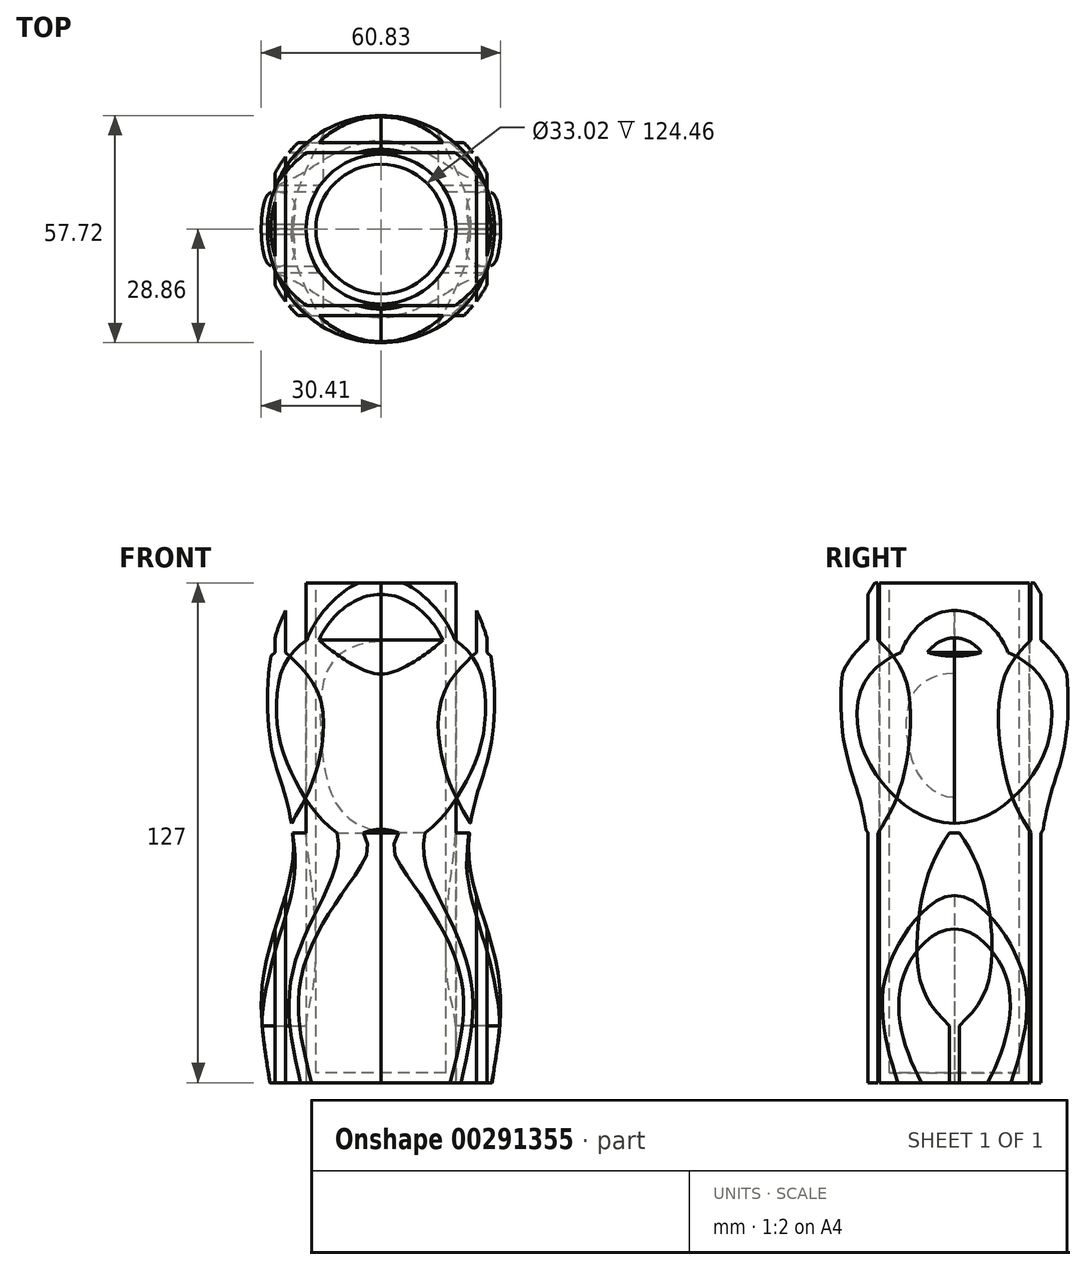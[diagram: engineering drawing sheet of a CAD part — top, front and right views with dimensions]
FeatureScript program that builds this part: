
annotation { "Feature Type Name" : "Feature", "Feature Type Description" : "" }
export const myFeature = defineFeature(function(context is Context, id is Id, definition is map)
    precondition{}
    {
        {
            var Q0;
            Q0=qCreatedBy(makeId("Right.planeOp"),FACE);
            var sketch = newSketch(context, id + "F0", { "sketchPlane" : qUnion([Q0])});
            skLineSegment(sketch, "E0.bottom", {"start": v(44.45, 63.5) * mm, "end": v(-44.45, 63.5) * mm});
            skLineSegment(sketch, "E0.top", {"start": v(44.45, -63.5) * mm, "end": v(-44.45, -63.5) * mm});
            skLineSegment(sketch, "E0.left", {"start": v(44.45, 63.5) * mm, "end": v(44.45, -63.5) * mm});
            skLineSegment(sketch, "E0.right", {"start": v(-44.45, 63.5) * mm, "end": v(-44.45, -63.5) * mm});
            skPoint(sketch, "E0.middle", {"position": v(0, 0) * mm});
            skLineSegment(sketch, "E1", {"start": v(0, 63.5) * mm, "end": v(-1.27, 63.5) * mm});
            skLineSegment(sketch, "E2", {"start": v(-1.27, 63.5) * mm, "end": v(-1.27, 0) * mm});
            skFitSpline(sketch, "E3", {"points": [v(-1.27, 0) * mm, v(-7.1, -11.9) * mm, v(-8.58, -38.04) * mm, v(-1.27, -49.01) * mm], "startDerivative": vector(-21.64, -33.6) * mm, "endDerivative": vector(30.34, -30.06) * mm});
            skLineSegment(sketch, "E4", {"start": v(-1.27, -49.01) * mm, "end": v(-1.27, -63.5) * mm});
            skLineSegment(sketch, "E5.MirrorCS", {"start": v(1.27, 63.5) * mm, "end": v(1.27, 0) * mm});
            skFitSpline(sketch, "E6.MirrorCS", {"points": [v(1.27, 0) * mm, v(7.1, -11.9) * mm, v(8.58, -38.04) * mm, v(1.27, -49.01) * mm], "startDerivative": vector(21.64, -33.6) * mm, "endDerivative": vector(-30.34, -30.06) * mm});
            skLineSegment(sketch, "E7.MirrorCS", {"start": v(1.27, -49.01) * mm, "end": v(1.27, -63.5) * mm});
            skPoint(sketch, "E8.end.orphan", {"position": v(0, -63.5) * mm});
            skLineSegment(sketch, "E9", {"start": v(-1.27, 0) * mm, "end": v(1.27, 0) * mm});
            skFitSpline(sketch, "E10.MirrorCS", {"points": [v(19.47, 0) * mm, v(13.64, 11.9) * mm, v(12.16, 38.04) * mm, v(19.47, 49.01) * mm], "startDerivative": vector(-21.64, 33.6) * mm, "endDerivative": vector(30.34, 30.06) * mm});
            skPoint(sketch, "E11.end.orphan", {"position": v(10.37, 0) * mm});
            skPoint(sketch, "E12.MirrorCS.end.orphan", {"position": v(1.27, 49.01) * mm});
            skPoint(sketch, "E13.trimOffspring.end.orphan", {"position": v(44.45, 0) * mm});
            skPoint(sketch, "E14.orphan", {"position": v(-44.45, 0) * mm});
            skLineSegment(sketch, "E15", {"start": v(19.47, 49.01) * mm, "end": v(19.47, 63.5) * mm});
            skLineSegment(sketch, "E16", {"start": v(19.47, 0) * mm, "end": v(19.47, -63.5) * mm});
            skLineSegment(sketch, "E17", {"start": v(19.47, -63.5) * mm, "end": v(20.74, -63.5) * mm});
            skLineSegment(sketch, "E18.MirrorCS", {"start": v(22.01, 49.01) * mm, "end": v(22.01, 63.5) * mm});
            skFitSpline(sketch, "E19.MirrorCS", {"points": [v(22.01, 0) * mm, v(27.84, 11.9) * mm, v(29.32, 38.04) * mm, v(22.01, 49.01) * mm], "startDerivative": vector(21.64, 33.6) * mm, "endDerivative": vector(-30.34, 30.06) * mm});
            skLineSegment(sketch, "E20.MirrorCS", {"start": v(22.01, 0) * mm, "end": v(22.01, -63.5) * mm});
            skPoint(sketch, "E21.end.orphan", {"position": v(20.74, 63.5) * mm});
            skFitSpline(sketch, "E22.MirrorCS", {"points": [v(-19.47, 0) * mm, v(-13.64, 11.9) * mm, v(-12.16, 38.04) * mm, v(-19.47, 49.01) * mm], "startDerivative": vector(21.64, 33.6) * mm, "endDerivative": vector(-30.34, 30.06) * mm});
            skFitSpline(sketch, "E23.MirrorCS", {"points": [v(-22.01, 0) * mm, v(-27.84, 11.9) * mm, v(-29.32, 38.04) * mm, v(-22.01, 49.01) * mm], "startDerivative": vector(-21.64, 33.6) * mm, "endDerivative": vector(30.34, 30.06) * mm});
            skLineSegment(sketch, "E24.MirrorCS", {"start": v(-22.01, 49.01) * mm, "end": v(-22.01, 63.5) * mm});
            skLineSegment(sketch, "E25.MirrorCS", {"start": v(-19.47, 49.01) * mm, "end": v(-19.47, 63.5) * mm});
            skLineSegment(sketch, "E26.MirrorCS", {"start": v(-19.47, 0) * mm, "end": v(-19.47, -63.5) * mm});
            skLineSegment(sketch, "E27.MirrorCS", {"start": v(-22.01, 0) * mm, "end": v(-22.01, -63.5) * mm});
            skSolve(sketch);
        }
        {
            var Q0;
            Q0=makeQuery(id+"F0.imprint","IMPRINT",FACE,{"disambiguationData":[TD([[makeQuery(id+"F0.imprint","IMPRINT",EDGE,{"derivedFrom":sQuery(id+"F0.wireOp",EDGE,"E22.MirrorCS")}),1.0]])]});
            var Q1;
            {var subQ1=sQuery(id+"F0.wireOp",EDGE,"E1");Q1=makeQuery(id+"F0.imprint","IMPRINT",FACE,{"disambiguationData":[TD([[makeQuery(id+"F0.imprint","IMPRINT",EDGE,{"derivedFrom":subQ1}),1.0]])]});}
            var Q2;
            Q2=makeQuery(id+"F0.imprint","IMPRINT",FACE,{"disambiguationData":[TD([[makeQuery(id+"F0.imprint","IMPRINT",EDGE,{"derivedFrom":sQuery(id+"F0.wireOp",EDGE,"E3")}),1.0]])]});
            var Q3;
            Q3=makeQuery(id+"F0.imprint","IMPRINT",FACE,{"disambiguationData":[TD([[makeQuery(id+"F0.imprint","IMPRINT",EDGE,{"derivedFrom":sQuery(id+"F0.wireOp",EDGE,"E10.MirrorCS")}),-1.0]])]});
            extrude(context, id + "F1", {"entities" : qUnion([Q0, Q1, Q2, Q3]), "depth" : 31.75 * mm});
        }
        {
            var Q0;
            Q0=makeQuery(id+"F1.opExtrude","CAP_FACE",FACE,{"disambiguationData":[OSD([sQuery(id+"F0.wireOp",EDGE,"E0.bottom"),sQuery(id+"F0.wireOp",EDGE,"E0.top"),sQuery(id+"F0.wireOp",EDGE,"E22.MirrorCS"),sQuery(id+"F0.wireOp",EDGE,"E23.MirrorCS"),sQuery(id+"F0.wireOp",EDGE,"E24.MirrorCS"),sQuery(id+"F0.wireOp",EDGE,"E25.MirrorCS"),sQuery(id+"F0.wireOp",EDGE,"E26.MirrorCS"),sQuery(id+"F0.wireOp",EDGE,"E27.MirrorCS")])],"isStart":true});
            var Q1;
            Q1=makeQuery(id+"F1.opExtrude","CAP_FACE",FACE,{"disambiguationData":[OSD([sQuery(id+"F0.wireOp",EDGE,"E0.bottom"),sQuery(id+"F0.wireOp",EDGE,"E0.top"),sQuery(id+"F0.wireOp",EDGE,"E1"),sQuery(id+"F0.wireOp",EDGE,"E2"),sQuery(id+"F0.wireOp",EDGE,"E3"),sQuery(id+"F0.wireOp",EDGE,"E4"),sQuery(id+"F0.wireOp",EDGE,"E5.MirrorCS"),sQuery(id+"F0.wireOp",EDGE,"E6.MirrorCS"),sQuery(id+"F0.wireOp",EDGE,"E7.MirrorCS")])],"isStart":true});
            var Q2;
            Q2=makeQuery(id+"F1.opExtrude","CAP_FACE",FACE,{"disambiguationData":[OSD([sQuery(id+"F0.wireOp",EDGE,"E0.bottom"),sQuery(id+"F0.wireOp",EDGE,"E0.top"),sQuery(id+"F0.wireOp",EDGE,"E10.MirrorCS"),sQuery(id+"F0.wireOp",EDGE,"E15"),sQuery(id+"F0.wireOp",EDGE,"E16"),sQuery(id+"F0.wireOp",EDGE,"E17"),sQuery(id+"F0.wireOp",EDGE,"E18.MirrorCS"),sQuery(id+"F0.wireOp",EDGE,"E19.MirrorCS"),sQuery(id+"F0.wireOp",EDGE,"E20.MirrorCS")])],"isStart":true});
            extrude(context, id + "F2", {"entities" : qUnion([Q0, Q1, Q2]), "depth" : 31.75 * mm});
        }
        {
            var Q0;
            Q0=qCreatedBy(makeId("Front.planeOp"),FACE);
            var sketch = newSketch(context, id + "F3", { "sketchPlane" : qUnion([Q0])});
            skLineSegment(sketch, "E28.bottom", {"start": v(63.5, 63.5) * mm, "end": v(-63.5, 63.5) * mm});
            skLineSegment(sketch, "E28.top", {"start": v(63.5, -63.5) * mm, "end": v(-63.5, -63.5) * mm});
            skLineSegment(sketch, "E28.left", {"start": v(63.5, 63.5) * mm, "end": v(63.5, -63.5) * mm});
            skLineSegment(sketch, "E28.right", {"start": v(-63.5, 63.5) * mm, "end": v(-63.5, -63.5) * mm});
            skPoint(sketch, "E28.middle", {"position": v(0, 0) * mm});
            skLineSegment(sketch, "E29", {"start": v(0, 63.5) * mm, "end": v(1.27, 63.5) * mm});
            skLineSegment(sketch, "E30", {"start": v(1.27, 63.5) * mm, "end": v(1.27, 0) * mm});
            skLineSegment(sketch, "E31", {"start": v(0, 0) * mm, "end": v(1.27, 0) * mm});
            skFitSpline(sketch, "E32", {"points": [v(1.27, 0) * mm, v(8.62, -14.28) * mm, v(10.1, -34) * mm, v(1.27, -45.84) * mm], "startDerivative": vector(25.04, -39.95) * mm, "endDerivative": vector(-35.1, -33.02) * mm});
            skLineSegment(sketch, "E33.trimOffspring", {"start": v(1.27, -45.84) * mm, "end": v(1.27, -63.5) * mm});
            skLineSegment(sketch, "E34.MirrorCS", {"start": v(-1.27, 63.5) * mm, "end": v(-1.27, 0) * mm});
            skFitSpline(sketch, "E35.MirrorCS", {"points": [v(-1.27, 0) * mm, v(-8.62, -14.28) * mm, v(-10.1, -34) * mm, v(-1.27, -45.84) * mm], "startDerivative": vector(-25.04, -39.95) * mm, "endDerivative": vector(35.1, -33.02) * mm});
            skLineSegment(sketch, "E36.MirrorCS", {"start": v(-1.27, -45.84) * mm, "end": v(-1.27, -63.5) * mm});
            skPoint(sketch, "E37.end.orphan", {"position": v(0, -63.5) * mm});
            skFitSpline(sketch, "E38.MirrorCS", {"points": [v(24.24, 0) * mm, v(16.9, 14.28) * mm, v(15.41, 34) * mm, v(24.24, 45.84) * mm], "startDerivative": vector(-25.04, 39.95) * mm, "endDerivative": vector(35.1, 33.02) * mm});
            skPoint(sketch, "E39.trimOffspring.end.orphan", {"position": v(63.5, 0) * mm});
            skPoint(sketch, "E40.orphan", {"position": v(-63.5, 0) * mm});
            skLineSegment(sketch, "E41", {"start": v(24.24, 45.84) * mm, "end": v(24.24, 63.5) * mm});
            skLineSegment(sketch, "E42", {"start": v(24.24, 63.5) * mm, "end": v(25.5, 63.5) * mm});
            skLineSegment(sketch, "E43", {"start": v(24.24, 0) * mm, "end": v(24.24, -63.5) * mm});
            skFitSpline(sketch, "E44.MirrorCS", {"points": [v(26.91, 0) * mm, v(34.26, 14.28) * mm, v(35.74, 34) * mm, v(26.91, 45.84) * mm], "startDerivative": vector(25.04, 39.95) * mm, "endDerivative": vector(-35.1, 33.02) * mm});
            skLineSegment(sketch, "E45.MirrorCS", {"start": v(26.91, 45.84) * mm, "end": v(26.91, 63.5) * mm});
            skLineSegment(sketch, "E46.MirrorCS", {"start": v(26.91, 0) * mm, "end": v(26.91, -63.5) * mm});
            skPoint(sketch, "E47.MirrorCS.end.orphan", {"position": v(1.27, 45.84) * mm});
            skLineSegment(sketch, "E48.MirrorCS", {"start": v(-24.24, 45.84) * mm, "end": v(-24.24, 63.5) * mm});
            skFitSpline(sketch, "E49.MirrorCS", {"points": [v(-24.24, 0) * mm, v(-16.9, 14.28) * mm, v(-15.41, 34) * mm, v(-24.24, 45.84) * mm], "startDerivative": vector(25.04, 39.95) * mm, "endDerivative": vector(-35.1, 33.02) * mm});
            skFitSpline(sketch, "E50.MirrorCS", {"points": [v(-26.91, 0) * mm, v(-34.26, 14.28) * mm, v(-35.74, 34) * mm, v(-26.91, 45.84) * mm], "startDerivative": vector(-25.04, 39.95) * mm, "endDerivative": vector(35.1, 33.02) * mm});
            skLineSegment(sketch, "E51.MirrorCS", {"start": v(-26.91, 0) * mm, "end": v(-26.91, -63.5) * mm});
            skLineSegment(sketch, "E52.MirrorCS", {"start": v(-24.24, 0) * mm, "end": v(-24.24, -63.5) * mm});
            skLineSegment(sketch, "E53", {"start": v(-26.91, 45.84) * mm, "end": v(-26.91, 63.5) * mm});
            skSolve(sketch);
        }
        {
            var Q0;
            Q0=makeQuery(id+"F3.imprint","IMPRINT",FACE,{"disambiguationData":[TD([[makeQuery(id+"F3.imprint","IMPRINT",EDGE,{"derivedFrom":sQuery(id+"F3.wireOp",EDGE,"E38.MirrorCS")}),-1.0]])]});
            var Q1;
            {var subQ0=sQuery(id+"F3.wireOp",EDGE,"E29");Q1=makeQuery(id+"F3.imprint","IMPRINT",FACE,{"disambiguationData":[TD([[makeQuery(id+"F3.imprint","IMPRINT",EDGE,{"derivedFrom":subQ0}),-1.0]])]});}
            var Q2;
            {var subQ3=sQuery(id+"F3.wireOp",EDGE,"E48.MirrorCS");Q2=makeQuery(id+"F3.imprint","IMPRINT",FACE,{"disambiguationData":[TD([[makeQuery(id+"F3.imprint","IMPRINT",EDGE,{"derivedFrom":subQ3}),1.0]])]});}
            extrude(context, id + "F4", {"entities" : qUnion([Q0, Q1, Q2]), "depth" : 31.75 * mm});
        }
        {
            var Q0;
            Q0=makeQuery(id+"F4.opExtrude","CAP_FACE",FACE,{"disambiguationData":[OSD([sQuery(id+"F3.wireOp",EDGE,"E28.bottom"),sQuery(id+"F3.wireOp",EDGE,"E28.top"),sQuery(id+"F3.wireOp",EDGE,"E38.MirrorCS"),sQuery(id+"F3.wireOp",EDGE,"E41"),sQuery(id+"F3.wireOp",EDGE,"E42"),sQuery(id+"F3.wireOp",EDGE,"E43"),sQuery(id+"F3.wireOp",EDGE,"E44.MirrorCS"),sQuery(id+"F3.wireOp",EDGE,"E45.MirrorCS"),sQuery(id+"F3.wireOp",EDGE,"E46.MirrorCS")])],"isStart":true});
            var Q1;
            Q1=makeQuery(id+"F4.opExtrude","CAP_FACE",FACE,{"disambiguationData":[OSD([sQuery(id+"F3.wireOp",EDGE,"E28.bottom"),sQuery(id+"F3.wireOp",EDGE,"E28.top"),sQuery(id+"F3.wireOp",EDGE,"E29"),sQuery(id+"F3.wireOp",EDGE,"E30"),sQuery(id+"F3.wireOp",EDGE,"E32"),sQuery(id+"F3.wireOp",EDGE,"E33.trimOffspring"),sQuery(id+"F3.wireOp",EDGE,"E34.MirrorCS"),sQuery(id+"F3.wireOp",EDGE,"E35.MirrorCS"),sQuery(id+"F3.wireOp",EDGE,"E36.MirrorCS")])],"isStart":true});
            var Q2;
            Q2=makeQuery(id+"F4.opExtrude","CAP_FACE",FACE,{"disambiguationData":[OSD([sQuery(id+"F3.wireOp",EDGE,"E28.bottom"),sQuery(id+"F3.wireOp",EDGE,"E28.top"),sQuery(id+"F3.wireOp",EDGE,"E48.MirrorCS"),sQuery(id+"F3.wireOp",EDGE,"E49.MirrorCS"),sQuery(id+"F3.wireOp",EDGE,"E50.MirrorCS"),sQuery(id+"F3.wireOp",EDGE,"E51.MirrorCS"),sQuery(id+"F3.wireOp",EDGE,"E52.MirrorCS"),sQuery(id+"F3.wireOp",EDGE,"E53")])],"isStart":true});
            extrude(context, id + "F5", {"entities" : qUnion([Q0, Q1, Q2]), "depth" : 31.75 * mm});
        }
        {
            var Q0;
            Q0=qCreatedBy(makeId("Right.planeOp"),FACE);
            var sketch = newSketch(context, id + "F6", { "sketchPlane" : qUnion([Q0])});
            skFitSpline(sketch, "E54", {"points": [v(-20.28, 63.5) * mm, v(-27.2, 48.45) * mm, v(-28.18, 23.74) * mm, v(-24.48, 9.9) * mm, v(-22.25, -3.7) * mm, v(-24.72, -17.53) * mm, v(-30.16, -38.53) * mm, v(-28.18, -63.5) * mm], "startDerivative": vector(-59.29, -98.47) * mm, "endDerivative": vector(25.4, -151.35) * mm});
            skPoint(sketch, "E55.end.orphan", {"position": v(0, 63.5) * mm});
            skPoint(sketch, "E55.start.orphan", {"position": v(0, -63.5) * mm});
            skLineSegment(sketch, "E56", {"start": v(-20.28, 63.5) * mm, "end": v(-49.67, 63.5) * mm});
            skLineSegment(sketch, "E57", {"start": v(-49.67, 63.5) * mm, "end": v(-49.67, -63.5) * mm});
            skLineSegment(sketch, "E58", {"start": v(-49.67, -63.5) * mm, "end": v(-28.18, -63.5) * mm});
            skSolve(sketch);
        }
        {
            var Q0;
            Q0=qCreatedBy(makeId("Right.planeOp"),FACE);
            var sketch = newSketch(context, id + "F7", { "sketchPlane" : qUnion([Q0])});
            skLineSegment(sketch, "E59", {"start": v(0, 63.35) * mm, "end": v(0, -63.24) * mm});
            skSolve(sketch);
        }
        {
            var Q0;
            Q0=makeQuery(id+"F6.imprint","IMPRINT",FACE,{"disambiguationData":[TD([[makeQuery(id+"F6.imprint","IMPRINT",EDGE,{"derivedFrom":sQuery(id+"F6.wireOp",EDGE,"E54")}),-1.0]])]});
            var Q1;
            Q1=sQuery(id+"F7.wireOp",EDGE,"E59");
            revolve(context, id + "F8", {"operationType" : NewBodyOperationType.REMOVE, "entities" : qUnion([Q0]), "axis" : qUnion([Q1]), "revolveType" : RevolveType.FULL, "oppositeDirection" : true});
        }
        {
            var Q0;
            Q0=qCreatedBy(makeId("Top.planeOp"),FACE);
            var sketch = newSketch(context, id + "F9", { "sketchPlane" : qUnion([Q0])});
            skCircle(sketch, "E60", {"center": v(0, 0) * mm, "radius": 19.05 * mm});
            skSolve(sketch);
        }
        {
            var Q0;
            Q0=makeQuery(id+"F9.imprint","IMPRINT",FACE,{"disambiguationData":[TD([[makeQuery(id+"F9.imprint","IMPRINT",EDGE,{"derivedFrom":sQuery(id+"F9.wireOp",EDGE,"E60")}),1.0]])]});
            extrude(context, id + "F10", {"entities" : qUnion([Q0]), "operationType" : NewBodyOperationType.REMOVE, "endBound" : BoundingType.SYMMETRIC, "depth" : 127 * mm});
        }
        {
            var Q0;
            Q0=qCreatedBy(makeId("Front.planeOp"),FACE);
            var sketch = newSketch(context, id + "F11", { "sketchPlane" : qUnion([Q0])});
            skLineSegment(sketch, "E61", {"start": v(0, 0) * mm, "end": v(0, 63.5) * mm});
            skLineSegment(sketch, "E62", {"start": v(0, 63.5) * mm, "end": v(0, -63.5) * mm});
            skLineSegment(sketch, "E63", {"start": v(0, -63.5) * mm, "end": v(-19.05, -63.5) * mm});
            skLineSegment(sketch, "E64", {"start": v(-19.05, -63.5) * mm, "end": v(-19.05, 63.5) * mm});
            skLineSegment(sketch, "E65", {"start": v(-19.05, 63.5) * mm, "end": v(-16.51, 63.5) * mm});
            skLineSegment(sketch, "E66", {"start": v(0, -63.5) * mm, "end": v(0, -60.96) * mm});
            skLineSegment(sketch, "E67", {"start": v(0, -60.96) * mm, "end": v(-16.5, -60.96) * mm});
            skLineSegment(sketch, "E68", {"start": v(-16.5, -60.96) * mm, "end": v(-16.51, 63.5) * mm});
            skSolve(sketch);
        }
        {
            var Q0;
            Q0 = qSketchRegion(id + "F11", true);
            var Q1;
            Q1=sQuery(id+"F11.wireOp",EDGE,"E62");
            revolve(context, id + "F12", {"entities" : qUnion([Q0]), "axis" : qUnion([Q1]), "revolveType" : RevolveType.FULL});
        }
    });
